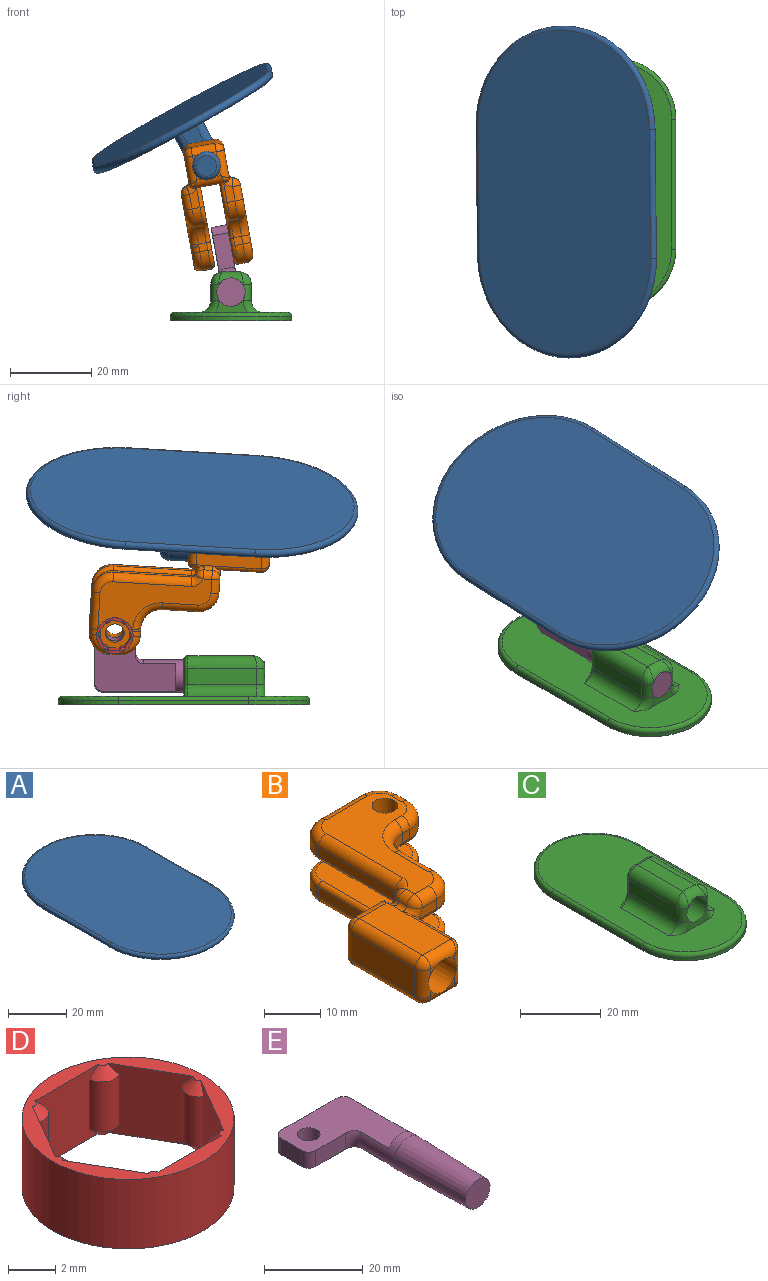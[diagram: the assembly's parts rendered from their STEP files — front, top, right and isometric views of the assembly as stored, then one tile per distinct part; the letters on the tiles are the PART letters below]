
ASSEMBLY  parts=5 mates=7
PART A: 19 faces, bbox 54.1x86.1x17.3 mm
  f0: plane 5.05x5.05mm, normal (0,-1,0), area 20mm2, adj f13
  f1: cone r=4mm half-angle=1.4deg, axis (0,1,0), area 449.9mm2, adj f2,f13
  f2: cylinder r=4mm len=8mm, axis (0,1,0), area 94.3mm2, adj f1,f3,f4,f5,f15,f17,f18
  f3: plane 7.54x4mm, normal (0,-1,0), area 28.7mm2, adj f2,f8,f17,f18
  f4: plane 11x1mm, normal (1,0,0), area 11mm2, adj f2,f8,f14,f18
  f5: plane 11x1mm, normal (-1,0,0), area 11mm2, adj f2,f8,f16,f17
  f6: plane 13x4mm, normal (0,1,0), area 50.3mm2, adj f8,f14,f15,f16
  f7: plane 80x48mm, normal (0,0,1), area 3345.6mm2, adj f9,f10,f11,f12
  f8: plane 80x48mm, normal (0,0,-1), area 3309mm2, adj f3,f4,f5,f6,f9,f10,f11,f12
  f9: torus R=24mm, axis (0,0,1), area 243.2mm2, adj f7,f8,f10,f11
  f10: cylinder r=1mm len=32mm, axis (0,1,0), area 100.5mm2, adj f7,f8,f9,f12
  f11: cylinder r=1mm len=32mm, axis (0,-1,0), area 100.5mm2, adj f7,f8,f9,f12
  f12: torus R=24mm, axis (0,0,1), area 243.2mm2, adj f7,f8,f10,f11
  f13: torus R=2.52mm, axis (0,-1,0), area 30.6mm2, adj f0,f1
  f14: cylinder r=2mm len=11mm, axis (0,0,1), area 34.6mm2, adj f4,f6,f8,f15
  f15: torus R=2mm, axis (0,1,0), area 32.3mm2, adj f2,f6,f14,f16
  f16: cylinder r=2mm len=11mm, axis (0,0,-1), area 34.6mm2, adj f5,f6,f8,f15
  f17: cylinder r=2mm len=11mm, axis (0,0,1), area 28.4mm2, adj f2,f3,f5,f8
  f18: cylinder r=2mm len=11mm, axis (0,0,-1), area 28.4mm2, adj f2,f3,f4,f8
PART B: 129 faces, bbox 33.2x44.1x15.2 mm
  f0: torus R=2mm, axis (0,0,-1), area 0mm2, adj f9,f93,f98,f99
  f1: torus R=2mm, axis (0,0,1), area 0mm2, adj f9,f88,f99,f100
  f2: plane 3x1.35mm, normal (0,1,0), area 1.2mm2, adj f14,f64,f99
  f3: plane 1.2x1.2mm, normal (0,-1,0), area 0.6mm2, adj f14,f66,f67
  f4: plane 1.2x1.2mm, normal (0,-1,0), area 0.6mm2, adj f14,f63,f67
  f5: plane 1.2x1.2mm, normal (0,-1,0), area 0.6mm2, adj f14,f61,f63
  f6: plane 3x1.35mm, normal (0,1,0), area 1.2mm2, adj f14,f73,f99
  f7: plane 0.35x0.35mm, normal (0,1,0), area 0.1mm2, adj f14,f70,f73
  f8: cylinder r=2.3mm len=4.6mm, axis (0,0,1), area 20.2mm2, adj f32,f33
  f9: plane 17.34x8.34mm, normal (1,0,0), area 115.3mm2, adj f0,f1,f24,f32,f63,f92,f97,f99
  f10: plane 0.35x0.35mm, normal (0,1,0), area 0.1mm2, adj f14,f64,f70
  f11: plane 16x6mm, normal (-1,0,0), area 96mm2, adj f65,f66,f70,f71
  f12: plane 1.2x1.2mm, normal (0,-1,0), area 0.6mm2, adj f14,f61,f66
  f13: plane 16.06x7.06mm, normal (0,0,1), area 111.9mm2, adj f48,f61,f64,f65,f88,f103
  f14: cone r=4mm half-angle=1.4deg, axis (0,1,0), area 469.7mm2, adj f2,f3,f4,f5,f6,f7,f10,f12
  f15: plane 16.06x7.06mm, normal (0,0,-1), area 111.9mm2, adj f45,f67,f71,f73,f93,f101
  f16: plane 5.04x2mm, normal (0,-1,0), area 8.2mm2, adj f40,f49,f92,f116
  f17: plane 8.7x2mm, normal (1,0,0), area 17.4mm2, adj f40,f41,f51,f114
  f18: plane 2x1.93mm, normal (0,-1,0), area 3.9mm2, adj f41,f42,f53,f112
  f19: plane 2.6x2mm, normal (1,0,0), area 5.2mm2, adj f42,f43,f55,f110
  f20: plane 10.46x2mm, normal (0,1,0), area 20.9mm2, adj f43,f44,f57,f108
  f21: plane 19.3x2mm, normal (-1,0,0), area 38.6mm2, adj f44,f47,f59,f106
  f22: cylinder r=2.3mm len=5mm, axis (0,0,-1), area 72.3mm2, adj f23,f24
  f23: plane 27.3x18.52mm, normal (0,0,1), area 218.6mm2, adj f22,f49,f50,f51,f52,f53,f54,f55
  f24: plane 29.3x21.46mm, normal (0,0,-1), area 308.3mm2, adj f9,f22,f105,f106,f107,f108,f109,f110
  f25: plane 19.3x2mm, normal (-1,0,0), area 38.6mm2, adj f39,f46,f75,f118
  f26: plane 10.46x2.01mm, normal (0,1,0), area 20.9mm2, adj f38,f39,f77,f78,f120
  f27: plane 2.68x2.61mm, normal (1,0,0), area 6.7mm2, adj f37,f38,f80,f122
  f28: plane 2.01x1.93mm, normal (0,-1,0), area 3.9mm2, adj f36,f37,f82,f83,f124
  f29: plane 8.7x2mm, normal (1,0,0), area 17.4mm2, adj f35,f36,f85,f126
  f30: plane 5.04x2mm, normal (0,-1,0), area 8.2mm2, adj f35,f87,f97,f128
  f31: plane 27.3x14.2mm, normal (0,0,-1), area 181.8mm2, adj f34,f74,f75,f76,f77,f83,f84,f85
  f32: plane 29.3x21.46mm, normal (0,0,1), area 308.3mm2, adj f8,f9,f117,f118,f119,f120,f121,f122
  f33: plane 9x9mm, normal (0,0,-1), area 47mm2, adj f8,f34
  f34: cylinder r=4.5mm len=9mm, axis (0,0,-1), area 101.8mm2, adj f31,f33,f78,f79,f80,f81,f82
  f35: cylinder r=5mm len=5mm, axis (0,0,1), area 15.7mm2, adj f29,f30,f86,f127
  f36: cylinder r=5mm len=5mm, axis (0,0,-1), area 15.7mm2, adj f28,f29,f84,f125
  f37: cylinder r=5mm len=5mm, axis (0,0,1), area 17.4mm2, adj f27,f28,f81,f123
  f38: cylinder r=5mm len=5mm, axis (0,0,1), area 17.4mm2, adj f26,f27,f79,f121
  f39: cylinder r=5mm len=5mm, axis (0,0,1), area 15.7mm2, adj f25,f26,f76,f119
  f40: cylinder r=5mm len=5mm, axis (0,0,-1), area 15.7mm2, adj f16,f17,f50,f115
  f41: cylinder r=5mm len=5mm, axis (0,0,1), area 15.7mm2, adj f17,f18,f52,f113
  f42: cylinder r=5mm len=5mm, axis (0,0,-1), area 15.7mm2, adj f18,f19,f54,f111
  f43: cylinder r=5mm len=5mm, axis (0,0,-1), area 15.7mm2, adj f19,f20,f56,f109
  f44: cylinder r=5mm len=5mm, axis (0,0,-1), area 15.7mm2, adj f20,f21,f58,f107
  f45: cylinder r=1mm len=2.76mm, axis (0,1,0), area 3.4mm2, adj f15,f93,f95,f97
  f46: cylinder r=1mm len=2mm, axis (0,0,-1), area 3mm2, adj f25,f74,f93,f117
  f47: cylinder r=1mm len=2mm, axis (0,0,1), area 3mm2, adj f21,f60,f88,f105
  f48: cylinder r=1mm len=2.76mm, axis (0,1,0), area 3.4mm2, adj f13,f88,f90,f92
  f49: cylinder r=2mm len=3.6mm, axis (-1,0,0), area 11.3mm2, adj f16,f23,f50,f91
  f50: torus R=3mm, axis (0,0,1), area 21.1mm2, adj f23,f40,f49,f51
  f51: cylinder r=2mm len=8.7mm, axis (0,-1,0), area 27.3mm2, adj f17,f23,f50,f52
  f52: torus R=7mm, axis (0,0,1), area 28.3mm2, adj f23,f41,f51,f53
  f53: cylinder r=2mm len=2mm, axis (-1,0,0), area 6.1mm2, adj f18,f23,f52,f54
  f54: torus R=3mm, axis (0,0,1), area 21.1mm2, adj f23,f42,f53,f55
  f55: cylinder r=2mm len=2.6mm, axis (0,-1,0), area 8.2mm2, adj f19,f23,f54,f56
  f56: torus R=3mm, axis (0,0,1), area 21.1mm2, adj f23,f43,f55,f57
  f57: cylinder r=2mm len=10.46mm, axis (1,0,0), area 32.9mm2, adj f20,f23,f56,f58
  f58: torus R=3mm, axis (0,0,1), area 21.1mm2, adj f23,f44,f57,f59
  f59: cylinder r=2mm len=19.3mm, axis (0,1,0), area 60.6mm2, adj f21,f23,f58,f60
  f60: torus R=3mm, axis (0,0,1), area 6.8mm2, adj f23,f47,f59,f89
  f61: cylinder r=2mm len=7mm, axis (-1,0,0), area 19.2mm2, adj f5,f12,f13,f14,f62,f104
  f62: sphere r=2mm, area 6.3mm2, adj f61,f65,f66
  f63: cylinder r=2mm len=8mm, axis (0,0,-1), area 20.8mm2, adj f4,f5,f9,f14,f102,f104
  f64: cylinder r=2mm len=7mm, axis (1,0,0), area 18.2mm2, adj f2,f10,f13,f14,f68,f88,f100
  f65: cylinder r=2mm len=16mm, axis (0,1,0), area 50.3mm2, adj f11,f13,f62,f68
  f66: cylinder r=2mm len=6mm, axis (0,0,1), area 17.6mm2, adj f3,f11,f12,f14,f62,f69
  f67: cylinder r=2mm len=7mm, axis (1,0,0), area 19.2mm2, adj f3,f4,f14,f15,f69,f102
  f68: sphere r=2mm, area 10.8mm2, adj f64,f65,f70
  f69: sphere r=2mm, area 6.3mm2, adj f66,f67,f71
  f70: cylinder r=2mm len=6mm, axis (0,0,-1), area 15.1mm2, adj f7,f10,f11,f14,f68,f72
  f71: cylinder r=2mm len=16mm, axis (0,-1,0), area 50.3mm2, adj f11,f15,f69,f72
  f72: sphere r=2mm, area 6.3mm2, adj f70,f71,f73
  f73: cylinder r=2mm len=7mm, axis (-1,0,0), area 18.2mm2, adj f6,f7,f14,f15,f72,f93,f98
  f74: torus R=3mm, axis (0,0,-1), area 6.8mm2, adj f31,f46,f75,f94
  f75: cylinder r=2mm len=19.3mm, axis (0,-1,0), area 60.6mm2, adj f25,f31,f74,f76
  f76: torus R=3mm, axis (0,0,-1), area 21.1mm2, adj f31,f39,f75,f77
  f77: cylinder r=2mm len=9.14mm, axis (-1,0,0), area 28.7mm2, adj f26,f31,f76,f78
  f78: bspline ~2.24x2.1mm, area 4mm2, adj f26,f34,f77,f79
  f79: bspline ~5x5mm, area 17.5mm2, adj f34,f38,f78,f80
  f80: bspline ~4.06x1.65mm, area 5mm2, adj f27,f34,f79,f81
  f81: bspline ~5x5mm, area 17.5mm2, adj f34,f37,f80,f82
  f82: bspline ~2.24x2.1mm, area 4mm2, adj f28,f34,f81,f83
  f83: cylinder r=2mm len=2mm, axis (1,0,0), area 1.9mm2, adj f28,f31,f82,f84
  f84: torus R=7mm, axis (0,0,-1), area 28.3mm2, adj f31,f36,f83,f85
  f85: cylinder r=2mm len=8.7mm, axis (0,1,0), area 27.3mm2, adj f29,f31,f84,f86
  f86: torus R=3mm, axis (0,0,-1), area 21.1mm2, adj f31,f35,f85,f87
  f87: cylinder r=2mm len=3.6mm, axis (1,0,0), area 11.3mm2, adj f30,f31,f86,f96
  f88: bspline ~3.98x2.96mm, area 7.7mm2, adj f1,f13,f47,f48,f64,f89,f100,f105
  f89: sphere r=2mm, area 4.8mm2, adj f60,f88,f90
  f90: cylinder r=2mm len=2.15mm, axis (0,1,0), area 5.9mm2, adj f23,f48,f89,f91
  f91: sphere r=2mm, area 5.7mm2, adj f49,f90,f92
  f92: torus R=3mm, axis (0,-1,0), area 5.2mm2, adj f9,f16,f48,f91,f103,f116
  f93: bspline ~3.98x2.96mm, area 7.7mm2, adj f0,f15,f45,f46,f73,f94,f98,f117
  f94: sphere r=2mm, area 3.4mm2, adj f74,f93,f95
  f95: cylinder r=2mm len=2.15mm, axis (0,1,0), area 5.9mm2, adj f31,f45,f94,f96
  f96: sphere r=2mm, area 5.7mm2, adj f87,f95,f97
  f97: torus R=3mm, axis (0,1,0), area 5.2mm2, adj f9,f30,f45,f96,f101,f128
  f98: torus R=1mm, axis (1,0,0), area 2mm2, adj f0,f73,f93,f99
  f99: cylinder r=1mm len=6.8mm, axis (0,0,1), area 9.5mm2, adj f0,f1,f2,f6,f9,f98,f100
  f100: torus R=1mm, axis (1,0,0), area 2mm2, adj f1,f64,f88,f99
  f101: cylinder r=1mm len=12mm, axis (0,1,0), area 17.4mm2, adj f9,f15,f97,f102
  f102: bspline ~2.39x2mm, area 2.2mm2, adj f63,f67,f101
  f103: cylinder r=1mm len=12mm, axis (0,-1,0), area 17.4mm2, adj f9,f13,f92,f104
  f104: bspline ~2.39x2mm, area 2.2mm2, adj f61,f63,f103
  f105: torus R=2mm, axis (0,0,1), area 5.3mm2, adj f9,f24,f47,f88,f106
  f106: cylinder r=1mm len=19.3mm, axis (0,-1,0), area 30.3mm2, adj f21,f24,f105,f107
  f107: torus R=4mm, axis (0,0,1), area 11.4mm2, adj f24,f44,f106,f108
  f108: cylinder r=1mm len=10.46mm, axis (-1,0,0), area 16.4mm2, adj f20,f24,f107,f109
  f109: torus R=4mm, axis (0,0,1), area 11.4mm2, adj f24,f43,f108,f110
  f110: cylinder r=1mm len=2.6mm, axis (0,1,0), area 4.1mm2, adj f19,f24,f109,f111
  f111: torus R=4mm, axis (0,0,1), area 11.4mm2, adj f24,f42,f110,f112
  f112: cylinder r=1mm len=1.93mm, axis (1,0,0), area 3mm2, adj f18,f24,f111,f113
  f113: torus R=6mm, axis (0,0,1), area 13.2mm2, adj f24,f41,f112,f114
  f114: cylinder r=1mm len=8.7mm, axis (0,1,0), area 13.7mm2, adj f17,f24,f113,f115
  f115: torus R=4mm, axis (0,0,1), area 11.4mm2, adj f24,f40,f114,f116
  f116: cylinder r=1mm len=5.54mm, axis (1,0,0), area 8.7mm2, adj f9,f16,f24,f92,f115
  f117: torus R=2mm, axis (0,0,-1), area 5.3mm2, adj f9,f32,f46,f93,f118
  f118: cylinder r=1mm len=19.3mm, axis (0,1,0), area 30.3mm2, adj f25,f32,f117,f119
  f119: torus R=4mm, axis (0,0,-1), area 11.4mm2, adj f32,f39,f118,f120
  f120: cylinder r=1mm len=10.46mm, axis (1,0,0), area 16.4mm2, adj f26,f32,f119,f121
  f121: torus R=4mm, axis (0,0,-1), area 11.4mm2, adj f32,f38,f120,f122
  f122: cylinder r=1mm len=2.6mm, axis (0,-1,0), area 4.1mm2, adj f27,f32,f121,f123
  f123: torus R=4mm, axis (0,0,-1), area 11.4mm2, adj f32,f37,f122,f124
  f124: cylinder r=1mm len=1.93mm, axis (-1,0,0), area 3mm2, adj f28,f32,f123,f125
  f125: torus R=6mm, axis (0,0,-1), area 13.2mm2, adj f32,f36,f124,f126
  f126: cylinder r=1mm len=8.7mm, axis (0,-1,0), area 13.7mm2, adj f29,f32,f125,f127
  f127: torus R=4mm, axis (0,0,-1), area 11.4mm2, adj f32,f35,f126,f128
  f128: cylinder r=1mm len=5.54mm, axis (-1,0,0), area 8.7mm2, adj f9,f30,f32,f97,f127
PART C: 42 faces, bbox 32.5x64.5x14.2 mm
  f0: plane 10.71x5mm, normal (0,1,0), area 17.4mm2, adj f4,f19,f35,f36,f40,f41
  f1: plane 4x4mm, normal (0,1,0), area 2.6mm2, adj f19,f38,f39,f40
  f2: plane 8x3.2mm, normal (0,-1,0), area 13.9mm2, adj f4,f19,f30,f31,f33,f34
  f3: plane 0.2x0.13mm, normal (0,-1,0), area 0mm2, adj f19,f27,f33
  f4: plane 60x28mm, normal (0,0,1), area 1199.4mm2, adj f0,f2,f20,f21,f22,f23,f24,f25
  f5: plane 62x30mm, normal (0,0,-1), area 1660.6mm2, adj f6,f7,f8,f9,f10,f12
  f6: cylinder r=15mm len=30mm, axis (0,0,-1), area 47.1mm2, adj f5,f7,f9,f21
  f7: plane 32x1mm, normal (-1,0,0), area 32mm2, adj f5,f6,f8,f20
  f8: cylinder r=15mm len=30mm, axis (0,0,-1), area 47.1mm2, adj f5,f7,f9,f22
  f9: plane 32x1mm, normal (1,0,0), area 32mm2, adj f5,f6,f8,f23
  f10: cylinder r=1mm len=2mm, axis (0,0,-1), area 6.3mm2, adj f5,f11
  f11: plane 2x2mm, normal (0,0,-1), area 3.1mm2, adj f10
  f12: cylinder r=1mm len=2mm, axis (0,0,-1), area 6.3mm2, adj f5,f13
  f13: plane 2x2mm, normal (0,0,-1), area 3.1mm2, adj f12
  f14: plane 17x4mm, normal (1,0,0), area 68mm2, adj f25,f26,f30,f36
  f15: plane 4x4mm, normal (0,1,0), area 2.6mm2, adj f19,f36,f37,f38
  f16: plane 17x4mm, normal (-1,0,0), area 68mm2, adj f24,f28,f33,f40
  f17: plane 0.2x0.13mm, normal (0,-1,0), area 0mm2, adj f19,f27,f30
  f18: plane 16x4mm, normal (0,0,1), area 64mm2, adj f26,f27,f28,f38
  f19: cone r=4mm half-angle=1.4deg, axis (0,1,0), area 469.9mm2, adj f0,f1,f2,f3,f15,f17,f27,f30
  f20: cylinder r=1mm len=32mm, axis (0,1,0), area 50.3mm2, adj f4,f7,f21,f22
  f21: torus R=14mm, axis (0,0,1), area 72.2mm2, adj f4,f6,f20,f23
  f22: torus R=14mm, axis (0,0,1), area 72.2mm2, adj f4,f8,f20,f23
  f23: cylinder r=1mm len=32mm, axis (0,-1,0), area 50.3mm2, adj f4,f9,f21,f22
  f24: cylinder r=3mm len=17mm, axis (0,-1,0), area 80.1mm2, adj f4,f16,f34,f41
  f25: cylinder r=3mm len=17mm, axis (0,1,0), area 80.1mm2, adj f4,f14,f31,f35
  f26: cylinder r=3mm len=17mm, axis (0,-1,0), area 78.4mm2, adj f14,f18,f29,f37
  f27: cylinder r=3mm len=6mm, axis (-1,0,0), area 18.6mm2, adj f3,f17,f18,f19,f29,f32
  f28: cylinder r=3mm len=17mm, axis (0,1,0), area 78.4mm2, adj f16,f18,f32,f39
  f29: bspline ~3.65x3mm, area 9.7mm2, adj f26,f27,f30
  f30: cylinder r=2mm len=4mm, axis (0,0,-1), area 11.3mm2, adj f2,f14,f17,f19,f29,f31
  f31: torus R=5mm, axis (0,-1,0), area 11.6mm2, adj f2,f4,f25,f30
  f32: bspline ~3.65x3mm, area 9.7mm2, adj f27,f28,f33
  f33: cylinder r=2mm len=4mm, axis (0,0,1), area 11.3mm2, adj f2,f3,f16,f19,f32,f34
  f34: torus R=5mm, axis (0,-1,0), area 11.6mm2, adj f2,f4,f24,f33
  f35: torus R=4mm, axis (0,-1,0), area 6.1mm2, adj f0,f4,f25,f36
  f36: cylinder r=1mm len=4mm, axis (0,0,1), area 6.3mm2, adj f0,f14,f15,f35,f37
  f37: torus R=2mm, axis (0,-1,0), area 6.5mm2, adj f15,f26,f36,f38
  f38: cylinder r=1mm len=4mm, axis (1,0,0), area 6.3mm2, adj f1,f15,f18,f37,f39
  f39: torus R=2mm, axis (0,-1,0), area 6.5mm2, adj f1,f28,f38,f40
  f40: cylinder r=1mm len=4mm, axis (0,0,-1), area 6.3mm2, adj f0,f1,f16,f39,f41
  f41: torus R=4mm, axis (0,-1,0), area 6.1mm2, adj f0,f4,f24,f40
PART D: 27 faces, bbox 9x9x3.6 mm
  f0: plane 9x9mm, normal (0,0,1), area 16.6mm2, adj f2,f3,f4,f5,f6,f7,f8,f10
  f1: plane 9x9mm, normal (0,0,-1), area 16.6mm2, adj f2,f3,f4,f5,f6,f7,f8,f11
  f2: plane 3.77x3.6mm, normal (0,-1,0), area 10.5mm2, adj f0,f1,f9,f10,f11,f18,f19,f20
  f3: plane 3.6x3.27mm, normal (-0.87,-0.5,0), area 10.5mm2, adj f0,f1,f9,f10,f11,f15,f16,f17
  f4: plane 3.6x3.27mm, normal (-0.87,0.5,0), area 10.5mm2, adj f0,f1,f12,f13,f14,f15,f16,f17
  f5: plane 3.77x3.6mm, normal (0,1,0), area 10.5mm2, adj f0,f1,f12,f13,f14,f24,f25,f26
  f6: plane 3.6x3.27mm, normal (0.87,0.5,0), area 10.5mm2, adj f0,f1,f21,f22,f23,f24,f25,f26
  f7: cylinder r=4.5mm len=9mm, axis (0,0,-1), area 101.8mm2, adj f0,f1
  f8: plane 3.6x3.27mm, normal (0.87,-0.5,0), area 10.5mm2, adj f0,f1,f18,f19,f20,f21,f22,f23
  f9: cylinder r=0.75mm len=2.6mm, axis (0,0,-1), area 4.1mm2, adj f2,f3,f10,f11
  f10: cone r=0.25mm half-angle=45deg, axis (0,0,-1), area 0.7mm2, adj f0,f2,f3,f9
  f11: cone r=0.75mm half-angle=45deg, axis (0,0,1), area 0.7mm2, adj f1,f2,f3,f9
  f12: cylinder r=0.75mm len=2.6mm, axis (0,0,-1), area 4.1mm2, adj f4,f5,f13,f14
  f13: cone r=0.25mm half-angle=45deg, axis (0,0,-1), area 0.7mm2, adj f0,f4,f5,f12
  f14: cone r=0.75mm half-angle=45deg, axis (0,0,1), area 0.7mm2, adj f1,f4,f5,f12
  f15: cone r=0.75mm half-angle=45deg, axis (0,0,1), area 0.7mm2, adj f1,f3,f4,f17
  f16: cone r=0.25mm half-angle=45deg, axis (0,0,-1), area 0.7mm2, adj f0,f3,f4,f17
  f17: cylinder r=0.75mm len=2.6mm, axis (0,0,-1), area 4.1mm2, adj f3,f4,f15,f16
  f18: cone r=0.75mm half-angle=45deg, axis (0,0,1), area 0.7mm2, adj f1,f2,f8,f20
  f19: cone r=0.25mm half-angle=45deg, axis (0,0,-1), area 0.7mm2, adj f0,f2,f8,f20
  f20: cylinder r=0.75mm len=2.6mm, axis (0,0,-1), area 4.1mm2, adj f2,f8,f18,f19
  f21: cone r=0.75mm half-angle=45deg, axis (0,0,1), area 0.7mm2, adj f1,f6,f8,f23
  f22: cone r=0.25mm half-angle=45deg, axis (0,0,-1), area 0.7mm2, adj f0,f6,f8,f23
  f23: cylinder r=0.75mm len=2.6mm, axis (0,0,-1), area 4.1mm2, adj f6,f8,f21,f22
  f24: cone r=0.75mm half-angle=45deg, axis (0,0,1), area 0.7mm2, adj f1,f5,f6,f26
  f25: cone r=0.25mm half-angle=45deg, axis (0,0,-1), area 0.7mm2, adj f0,f5,f6,f26
  f26: cylinder r=0.75mm len=2.6mm, axis (0,0,-1), area 4.1mm2, adj f5,f6,f24,f25
PART E: 15 faces, bbox 21.1x42.2x8.9 mm
  f0: plane 6.93x2mm, normal (0,1,0), area 9.8mm2, adj f3,f6
  f1: plane 7x7mm, normal (0,-1,0), area 38.5mm2, adj f2
  f2: cone r=4mm half-angle=1.4deg, axis (0,1,0), area 471.4mm2, adj f1,f3
  f3: cylinder r=4mm len=20mm, axis (0,1,0), area 159.2mm2, adj f0,f2,f4,f5,f6,f12,f14
  f4: plane 6.93x2mm, normal (0,1,0), area 9.8mm2, adj f3,f5
  f5: plane 20.21x20.21mm, normal (0,0,-1), area 250.9mm2, adj f3,f4,f7,f8,f9,f10,f11,f12
  f6: plane 20.21x20.21mm, normal (0,0,1), area 250.9mm2, adj f0,f3,f7,f8,f9,f10,f11,f12
  f7: plane 6x4mm, normal (-1,0,0), area 24mm2, adj f5,f6,f11,f13
  f8: plane 16.54x4mm, normal (0,1,0), area 64.4mm2, adj f5,f6,f12,f13
  f9: plane 8.88x4mm, normal (0,-1,0), area 34.6mm2, adj f5,f6,f11,f14
  f10: cylinder r=2.3mm len=4.6mm, axis (0,0,1), area 57.8mm2, adj f5,f6
  f11: cylinder r=2mm len=4mm, axis (0,0,1), area 12.6mm2, adj f5,f6,f7,f9
  f12: torus R=2mm, axis (0,1,0), area 13.9mm2, adj f3,f5,f6,f8
  f13: cylinder r=2mm len=4mm, axis (0,0,-1), area 12.6mm2, adj f5,f6,f7,f8
  f14: torus R=6mm, axis (0,1,0), area 12.6mm2, adj f3,f5,f6,f9
PLACE A rot(axis=(0.12,-0.99,-0.01),28.9deg) t=(97.09,-0.93,33.2)mm
PLACE B rot(axis=(0.03,1,0.04),79.8deg) t=(91.3,0.19,13.53)mm
PLACE C at identity fixed
PLACE D rot(axis=(-0.59,-0.63,0.5),124.3deg) t=(93.81,17,17.6)mm
PLACE E rot(axis=(0,1,0),79.7deg) t=(93.11,0,5.75)mm
MATE planar A.f13 <-> B.f14  axis (0.01,-1,-0.06) through (93.95,-21.29,38.13)mm
MATE fastened D.f7 <-> B.f8  axis (0.98,0,0.18) through (93.81,17,17.6)mm
MATE planar E.f2 <-> C.f19  axis (0,-1,0) through (100,-20,7)mm
MATE cylindrical A.f13 <-> B.f14  axis (0.01,-1,-0.06) through (93.95,-21.29,38.13)mm
MATE planar B.f39 <-> E.f6  axis (-0.98,0,-0.18) through (98.03,17.66,29.06)mm
MATE cylindrical E.f2 <-> C.f19  axis (0,-1,0) through (100,-20,7)mm
MATE cylindrical B.f8 <-> E.f10  axis (-0.98,0,-0.18) through (99.91,17,18.71)mm
